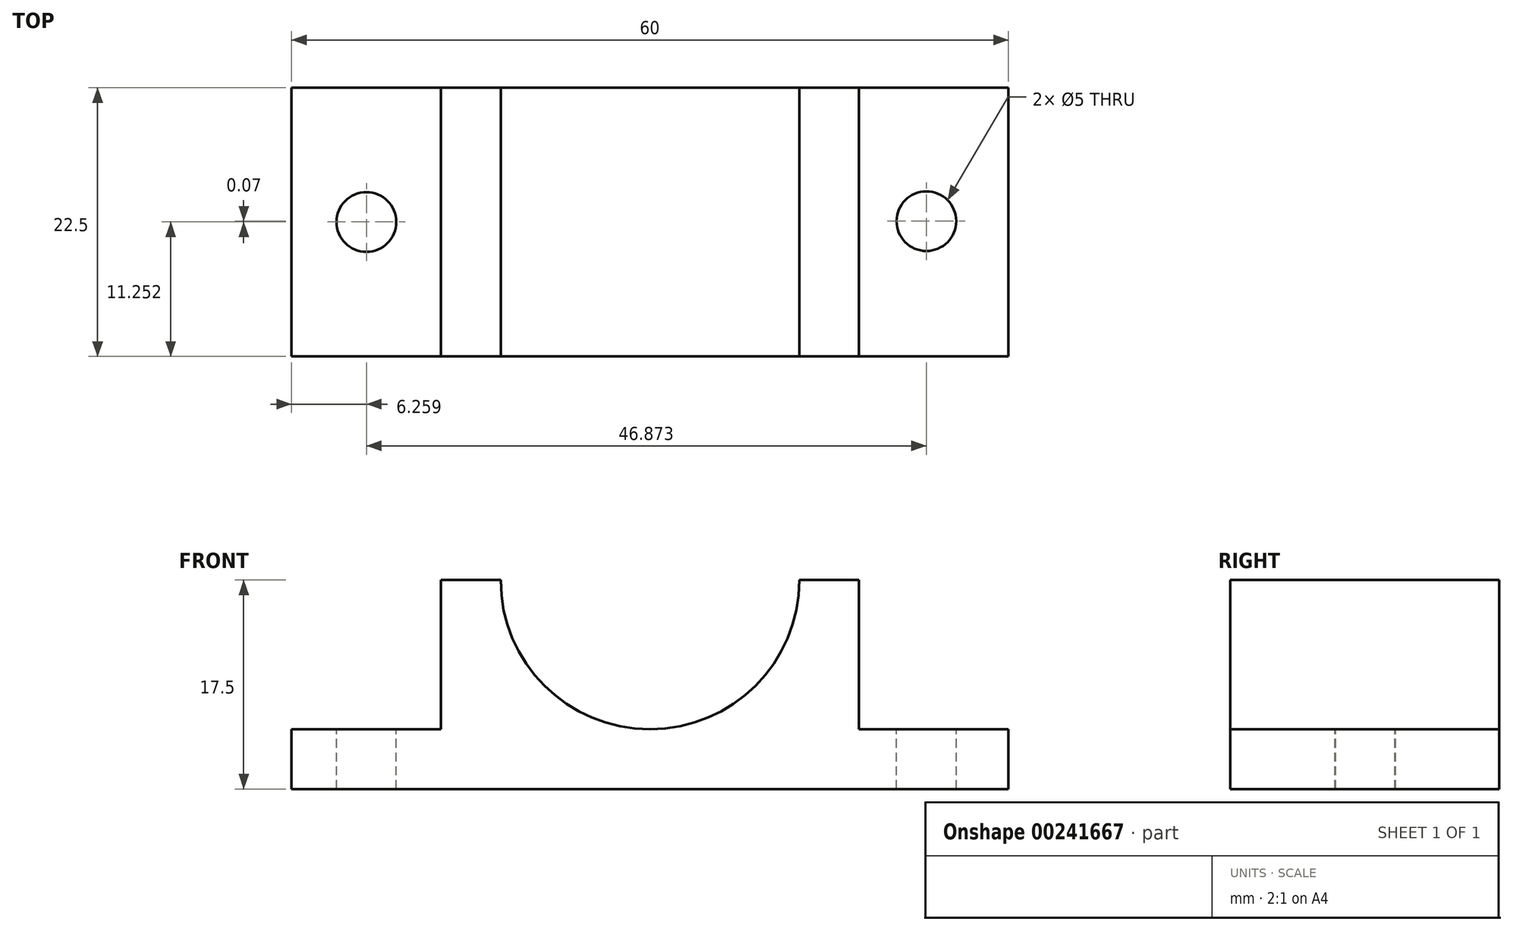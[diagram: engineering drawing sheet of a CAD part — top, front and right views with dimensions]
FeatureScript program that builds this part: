
annotation { "Feature Type Name" : "Feature", "Feature Type Description" : "" }
export const myFeature = defineFeature(function(context is Context, id is Id, definition is map)
    precondition{}
    {
        {
            var Q0;
            Q0=qCreatedBy(makeId("Top.planeOp"),FACE);
            var sketch = newSketch(context, id + "F0", { "sketchPlane" : qUnion([Q0])});
            skLineSegment(sketch, "E0.bottom", {"start": v(-4.67, -10.57) * mm, "end": v(55.33, -10.57) * mm});
            skLineSegment(sketch, "E0.top", {"start": v(-4.67, -33.07) * mm, "end": v(55.33, -33.07) * mm});
            skLineSegment(sketch, "E0.left", {"start": v(-4.67, -10.57) * mm, "end": v(-4.67, -33.07) * mm});
            skLineSegment(sketch, "E0.right", {"start": v(55.33, -10.57) * mm, "end": v(55.33, -33.07) * mm});
            skSolve(sketch);
        }
        {
            var Q0;
            Q0=makeQuery(id+"F0.imprint","IMPRINT",FACE,{"disambiguationData":[TD([[makeQuery(id+"F0.imprint","IMPRINT",EDGE,{"derivedFrom":sQuery(id+"F0.wireOp",EDGE,"E0.bottom")}),-1.0]])]});
            extrude(context, id + "F1", {"entities" : qUnion([Q0]), "depth" : 5 * mm});
        }
        {
            var Q0;
            Q0=makeQuery(id+"F1.opExtrude","CAP_FACE",FACE,{"disambiguationData":[OSD([sQuery(id+"F0.wireOp",EDGE,"E0.bottom"),sQuery(id+"F0.wireOp",EDGE,"E0.top"),sQuery(id+"F0.wireOp",EDGE,"E0.left"),sQuery(id+"F0.wireOp",EDGE,"E0.right")])],"isStart":false});
            var sketch = newSketch(context, id + "F2", { "sketchPlane" : qUnion([Q0])});
            skLineSegment(sketch, "E1", {"start": v(42.83, -18.3) * mm, "end": v(42.83, -10.57) * mm});
            skLineSegment(sketch, "E2", {"start": v(42.83, -18.3) * mm, "end": v(42.83, -33.07) * mm});
            skLineSegment(sketch, "E3", {"start": v(7.83, -21.82) * mm, "end": v(7.83, -10.57) * mm});
            skLineSegment(sketch, "E4", {"start": v(7.83, -21.82) * mm, "end": v(7.83, -33.07) * mm});
            skSolve(sketch);
        }
        {
            var Q0;
            {var subQ3=sQuery(id+"F2.wireOp",EDGE,"E1");Q0=makeQuery(id+"F2.imprint","IMPRINT",FACE,{"disambiguationData":[TD([[makeQuery(id+"F2.imprint","IMPRINT",EDGE,{"derivedFrom":subQ3}),1.0]])]});}
            extrude(context, id + "F3", {"entities" : qUnion([Q0]), "operationType" : NewBodyOperationType.ADD, "depth" : 12.5 * mm});
        }
        {
            var Q0;
            {var subQ0=sQuery(id+"F0.wireOp",EDGE,"E0.top");Q0=makeQuery(id+"F3.boolean.opBoolean","MERGE",FACE,{"derivedFrom":[makeQuery(id+"F1.opExtrude","SWEPT_FACE",FACE,{"disambiguationData":[OSD([subQ0])]}),makeQuery(id+"F3.opExtrude","SWEPT_FACE",FACE,{"disambiguationData":[OSD([subQ0])]})]});}
            var sketch = newSketch(context, id + "F4", { "sketchPlane" : qUnion([Q0])});
            skCircle(sketch, "E5", {"center": v(25.33, 17.5) * mm, "radius": 12.5 * mm});
            skSolve(sketch);
        }
        {
            var Q0;
            {var subQ0=sQuery(id+"F4.wireOp",EDGE,"E5");var subQ1=makeQuery(id+"F3.opExtrude","CAP_EDGE",EDGE,{"disambiguationData":[OSD([sQuery(id+"F0.wireOp",EDGE,"E0.top")])],"isStart":false});var subQ2=makeQuery(id+"F4.imprint","INTERSECT",VERTEX,{"disambiguationData":[OD(0.0)],"derivedFrom":[subQ1,subQ0]});Q0=makeQuery(id+"F4.imprint","IMPRINT",FACE,{"disambiguationData":[TD([[makeQuery(id+"F4.imprint","IMPRINT",EDGE,{"disambiguationData":[TD([[subQ2,1.0]])],"derivedFrom":subQ0}),1.0]])]});}
            extrude(context, id + "F5", {"entities" : qUnion([Q0]), "operationType" : NewBodyOperationType.REMOVE, "endBound" : BoundingType.THROUGH_ALL, "oppositeDirection" : true, "depth" : 25 * mm});
        }
        {
            var Q0;
            {var subQ0=sQuery(id+"F0.wireOp",EDGE,"E0.left");var subQ1=sQuery(id+"F0.wireOp",EDGE,"E0.top");var subQ2=sQuery(id+"F0.wireOp",EDGE,"E0.bottom");Q0=makeQuery(id+"F3.boolean.opBoolean","SPLIT",FACE,{"disambiguationData":[TD([makeQuery(id+"F1.opExtrude","SWEPT_FACE",FACE,{"disambiguationData":[OSD([subQ0])]})])],"derivedFrom":makeQuery(id+"F1.opExtrude","CAP_FACE",FACE,{"disambiguationData":[OSD([subQ2,subQ1,subQ0,sQuery(id+"F0.wireOp",EDGE,"E0.right")])],"isStart":false})});}
            var sketch = newSketch(context, id + "F6", { "sketchPlane" : qUnion([Q0])});
            skCircle(sketch, "E6", {"center": v(1.59, -21.82) * mm, "radius": 2.5 * mm});
            skPoint(sketch, "E6.centerSnap0", {"position": v(7.83, -21.82) * mm});
            skCircle(sketch, "E7", {"center": v(48.46, -21.75) * mm, "radius": 2.5 * mm});
            skSolve(sketch);
        }
        {
            var Q0;
            Q0=makeQuery(id+"F6.imprint","IMPRINT",FACE,{"disambiguationData":[TD([[makeQuery(id+"F6.imprint","IMPRINT",EDGE,{"derivedFrom":sQuery(id+"F6.wireOp",EDGE,"E6")}),1.0]])]});
            var Q1;
            Q1=makeQuery(id+"F6.imprint","IMPRINT",FACE,{"disambiguationData":[TD([[makeQuery(id+"F6.imprint","IMPRINT",EDGE,{"derivedFrom":sQuery(id+"F6.wireOp",EDGE,"E7")}),1.0]])]});
            extrude(context, id + "F7", {"entities" : qUnion([Q0, Q1]), "operationType" : NewBodyOperationType.REMOVE, "endBound" : BoundingType.THROUGH_ALL, "oppositeDirection" : true, "depth" : 25 * mm});
        }
    });
